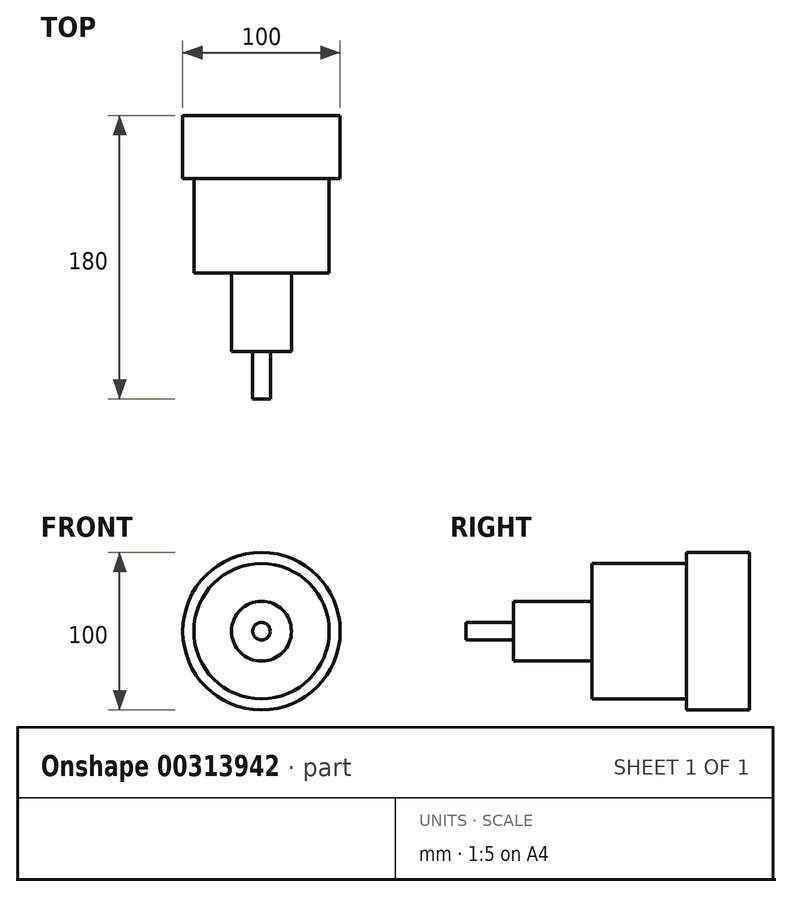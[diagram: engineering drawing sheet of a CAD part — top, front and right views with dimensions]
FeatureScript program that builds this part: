
annotation { "Feature Type Name" : "Feature", "Feature Type Description" : "" }
export const myFeature = defineFeature(function(context is Context, id is Id, definition is map)
    precondition{}
    {
        {
            var Q0;
            Q0=qCreatedBy(makeId("Front.planeOp"),FACE);
            var sketch = newSketch(context, id + "F0", { "sketchPlane" : qUnion([Q0])});
            skCircle(sketch, "E0", {"center": v(0, 0) * mm, "radius": 50 * mm});
            skSolve(sketch);
        }
        {
            var Q0;
            Q0 = qSketchRegion(id + "F0", true);
            extrude(context, id + "F1", {"entities" : qUnion([Q0]), "depth" : 40 * mm});
        }
        {
            var Q0;
            Q0=qCreatedBy(makeId("Front.planeOp"),FACE);
            var sketch = newSketch(context, id + "F2", { "sketchPlane" : qUnion([Q0])});
            skCircle(sketch, "E1", {"center": v(0, 0) * mm, "radius": 42.98 * mm});
            skSolve(sketch);
        }
        {
            var Q0;
            Q0 = qSketchRegion(id + "F2", true);
            extrude(context, id + "F3", {"entities" : qUnion([Q0]), "operationType" : NewBodyOperationType.ADD, "depth" : 100 * mm});
        }
        {
            var Q0;
            Q0=makeQuery(id+"F3.opExtrude","CAP_FACE",FACE,{"disambiguationData":[OSD([sQuery(id+"F2.wireOp",EDGE,"E1")])],"isStart":false});
            var sketch = newSketch(context, id + "F4", { "sketchPlane" : qUnion([Q0])});
            skCircle(sketch, "E2", {"center": v(0, 0) * mm, "radius": 19 * mm});
            skSolve(sketch);
        }
        {
            var Q0;
            Q0 = qSketchRegion(id + "F4", true);
            extrude(context, id + "F5", {"entities" : qUnion([Q0]), "operationType" : NewBodyOperationType.ADD, "depth" : 50 * mm});
        }
        {
            var Q0;
            Q0=makeQuery(id+"F5.opExtrude","CAP_FACE",FACE,{"disambiguationData":[OSD([sQuery(id+"F4.wireOp",EDGE,"E2")])],"isStart":false});
            var sketch = newSketch(context, id + "F6", { "sketchPlane" : qUnion([Q0])});
            skCircle(sketch, "E3", {"center": v(0, 0) * mm, "radius": 5.6 * mm});
            skSolve(sketch);
        }
        {
            var Q0;
            Q0 = qSketchRegion(id + "F6", true);
            extrude(context, id + "F7", {"entities" : qUnion([Q0]), "operationType" : NewBodyOperationType.ADD, "depth" : 30 * mm});
        }
    });
